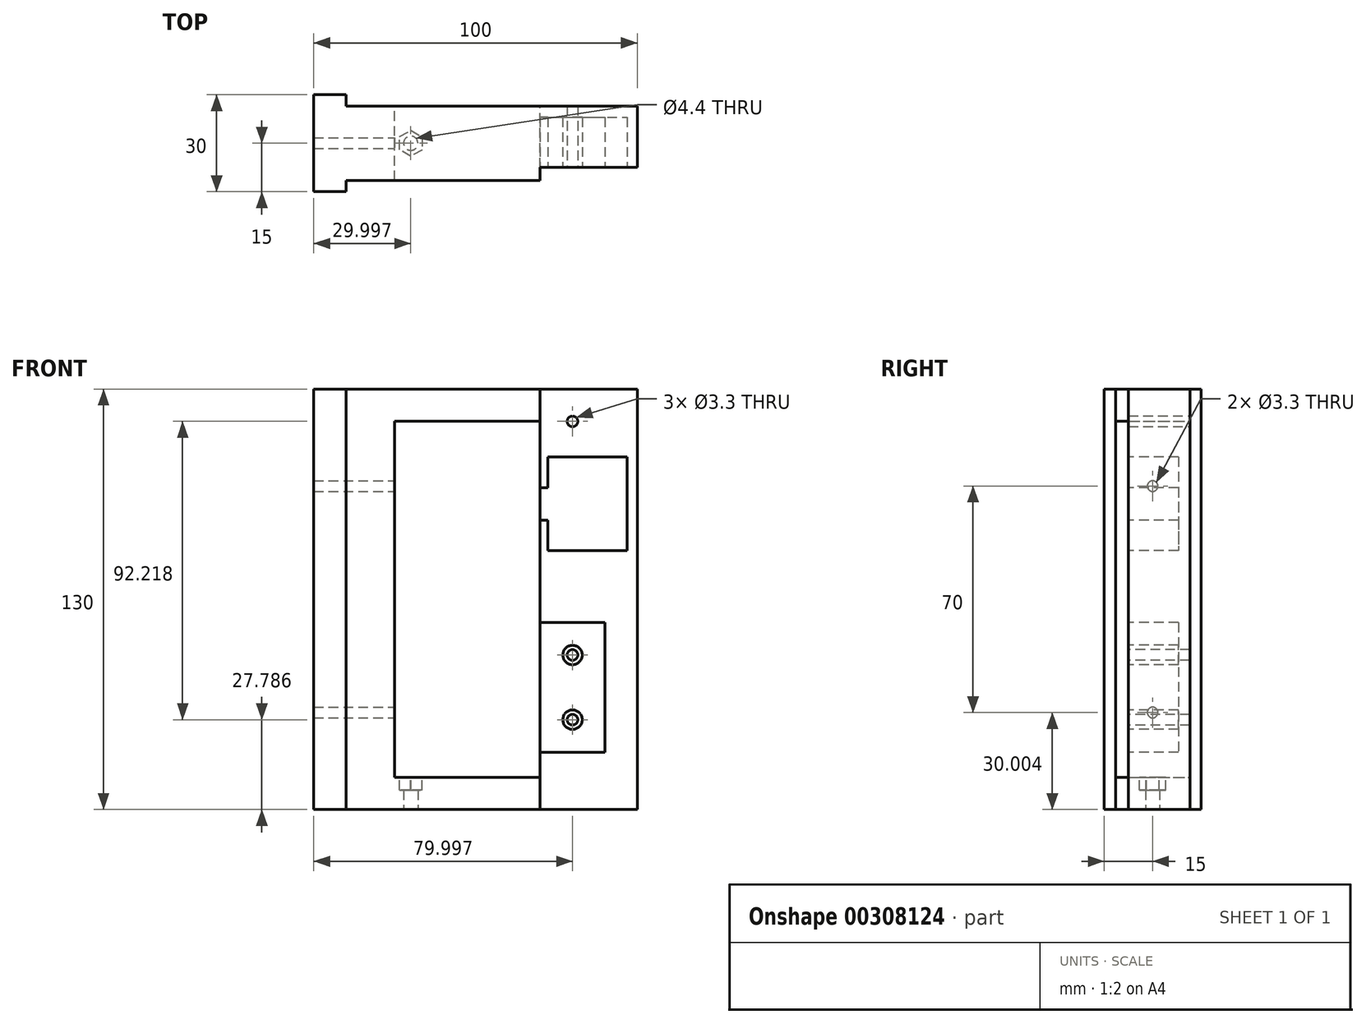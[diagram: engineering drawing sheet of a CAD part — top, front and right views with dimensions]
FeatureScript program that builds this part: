
annotation { "Feature Type Name" : "Feature", "Feature Type Description" : "" }
export const myFeature = defineFeature(function(context is Context, id is Id, definition is map)
    precondition{}
    {
        {
            var Q0;
            Q0=qCreatedBy(makeId("Front.planeOp"),FACE);
            var sketch = newSketch(context, id + "F0", { "sketchPlane" : qUnion([Q0])});
            skLineSegment(sketch, "E0", {"start": v(-34.7, 86.92) * mm, "end": v(-34.7, -43.08) * mm});
            skLineSegment(sketch, "E1", {"start": v(-34.7, -43.08) * mm, "end": v(55.3, -43.08) * mm});
            skLineSegment(sketch, "E2", {"start": v(55.3, -43.08) * mm, "end": v(55.3, 86.92) * mm});
            skLineSegment(sketch, "E3", {"start": v(55.3, 86.92) * mm, "end": v(-34.7, 86.92) * mm});
            skLineSegment(sketch, "E4.bottom", {"start": v(-19.7, 76.92) * mm, "end": v(25.3, 76.92) * mm});
            skLineSegment(sketch, "E4.top", {"start": v(-19.7, -33.08) * mm, "end": v(25.3, -33.08) * mm});
            skLineSegment(sketch, "E4.left", {"start": v(-19.7, 76.92) * mm, "end": v(-19.7, -33.08) * mm});
            skLineSegment(sketch, "E4.right", {"start": v(25.3, 76.92) * mm, "end": v(25.3, -33.08) * mm});
            skSolve(sketch);
        }
        {
            var Q0;
            Q0=makeQuery(id+"F0.imprint","IMPRINT",FACE,{"disambiguationData":[TD([[makeQuery(id+"F0.imprint","IMPRINT",EDGE,{"derivedFrom":sQuery(id+"F0.wireOp",EDGE,"E0")}),1.0]])]});
            extrude(context, id + "F1", {"entities" : qUnion([Q0]), "depth" : 23 * mm});
        }
        {
            var Q0;
            Q0=makeQuery(id+"F1.opExtrude","SWEPT_FACE",FACE,{"disambiguationData":[OSD([sQuery(id+"F0.wireOp",EDGE,"E0")])]});
            var sketch = newSketch(context, id + "F2", { "sketchPlane" : qUnion([Q0])});
            skLineSegment(sketch, "E5", {"start": v(23, 86.92) * mm, "end": v(26.5, 86.92) * mm});
            skLineSegment(sketch, "E6", {"start": v(26.5, 86.92) * mm, "end": v(26.5, -43.08) * mm});
            skLineSegment(sketch, "E7", {"start": v(26.5, -43.08) * mm, "end": v(23, -43.08) * mm});
            skLineSegment(sketch, "E8", {"start": v(23, -43.08) * mm, "end": v(0, -43.08) * mm});
            skLineSegment(sketch, "E9", {"start": v(0, -43.08) * mm, "end": v(-3.5, -43.08) * mm});
            skLineSegment(sketch, "E10", {"start": v(-3.5, -43.08) * mm, "end": v(-3.5, 86.92) * mm});
            skLineSegment(sketch, "E11", {"start": v(-3.5, 86.92) * mm, "end": v(0, 86.92) * mm});
            skSolve(sketch);
        }
        {
            var Q0;
            Q0=makeQuery(id+"F2.imprint","IMPRINT",FACE,{"disambiguationData":[TD([[makeQuery(id+"F2.imprint","IMPRINT",EDGE,{"derivedFrom":sQuery(id+"F2.wireOp",EDGE,"E9")}),-1.0]])]});
            var Q1;
            Q1=makeQuery(id+"F2.imprint","IMPRINT",FACE,{"disambiguationData":[TD([[makeQuery(id+"F2.imprint","IMPRINT",EDGE,{"derivedFrom":sQuery(id+"F2.wireOp",EDGE,"E8")}),-1.0]])]});
            var Q2;
            Q2=makeQuery(id+"F2.imprint","IMPRINT",FACE,{"disambiguationData":[TD([[makeQuery(id+"F2.imprint","IMPRINT",EDGE,{"derivedFrom":sQuery(id+"F2.wireOp",EDGE,"E5")}),-1.0]])]});
            extrude(context, id + "F3", {"entities" : qUnion([Q0, Q1, Q2]), "operationType" : NewBodyOperationType.ADD, "depth" : 10 * mm});
        }
        {
            var Q0;
            Q0=makeQuery(id+"F1.opExtrude","CAP_FACE",FACE,{"disambiguationData":[OSD([sQuery(id+"F0.wireOp",EDGE,"E0"),sQuery(id+"F0.wireOp",EDGE,"E1"),sQuery(id+"F0.wireOp",EDGE,"E2"),sQuery(id+"F0.wireOp",EDGE,"E3"),sQuery(id+"F0.wireOp",EDGE,"E4.bottom"),sQuery(id+"F0.wireOp",EDGE,"E4.top"),sQuery(id+"F0.wireOp",EDGE,"E4.left"),sQuery(id+"F0.wireOp",EDGE,"E4.right")])],"isStart":false});
            var sketch = newSketch(context, id + "F4", { "sketchPlane" : qUnion([Q0])});
            skLineSegment(sketch, "E12.bottom", {"start": v(55.3, 86.92) * mm, "end": v(25.3, 86.92) * mm});
            skLineSegment(sketch, "E12.top", {"start": v(55.3, -43.08) * mm, "end": v(25.3, -43.08) * mm});
            skLineSegment(sketch, "E12.left", {"start": v(55.3, 86.92) * mm, "end": v(55.3, -43.08) * mm});
            skLineSegment(sketch, "E12.right", {"start": v(25.3, 86.92) * mm, "end": v(25.3, -43.08) * mm});
            skSolve(sketch);
        }
        {
            var Q0;
            {var subQ2=sQuery(id+"F4.wireOp",EDGE,"E12.bottom");Q0=makeQuery(id+"F4.imprint","IMPRINT",FACE,{"disambiguationData":[TD([[makeQuery(id+"F4.imprint","IMPRINT",EDGE,{"derivedFrom":subQ2}),1.0]])]});}
            extrude(context, id + "F5", {"entities" : qUnion([Q0]), "operationType" : NewBodyOperationType.REMOVE, "oppositeDirection" : true, "depth" : 4 * mm});
        }
        {
            var Q0;
            Q0=makeQuery(id+"F5.boolean.opBoolean","COPY",FACE,{"derivedFrom":makeQuery(id+"F5.opExtrude","CAP_FACE",FACE,{"disambiguationData":[OSD([sQuery(id+"F4.wireOp",EDGE,"E12.bottom"),sQuery(id+"F4.wireOp",EDGE,"E12.top"),sQuery(id+"F4.wireOp",EDGE,"E12.left"),sQuery(id+"F4.wireOp",EDGE,"E12.right")])],"isStart":false})});
            var sketch = newSketch(context, id + "F6", { "sketchPlane" : qUnion([Q0])});
            skLineSegment(sketch, "E13.bottom", {"start": v(27.63, 65.92) * mm, "end": v(52.13, 65.92) * mm});
            skLineSegment(sketch, "E13.top", {"start": v(27.63, 36.92) * mm, "end": v(52.13, 36.92) * mm});
            skLineSegment(sketch, "E13.left", {"start": v(27.63, 65.92) * mm, "end": v(27.63, 36.92) * mm});
            skLineSegment(sketch, "E13.right", {"start": v(52.13, 65.92) * mm, "end": v(52.13, 36.92) * mm});
            skLineSegment(sketch, "E14.bottom", {"start": v(33.13, 56.42) * mm, "end": v(22.13, 56.42) * mm});
            skLineSegment(sketch, "E14.top", {"start": v(33.13, 46.42) * mm, "end": v(22.13, 46.42) * mm});
            skLineSegment(sketch, "E14.left", {"start": v(33.13, 56.42) * mm, "end": v(33.13, 46.42) * mm});
            skLineSegment(sketch, "E14.right", {"start": v(22.13, 56.42) * mm, "end": v(22.13, 46.42) * mm});
            skPoint(sketch, "E14.middle", {"position": v(27.63, 51.42) * mm});
            skLineSegment(sketch, "E15.bottom", {"start": v(52.13, 36.92) * mm, "end": v(42.13, 36.92) * mm});
            skLineSegment(sketch, "E15.top", {"start": v(52.13, 26.92) * mm, "end": v(42.13, 26.92) * mm});
            skLineSegment(sketch, "E15.left", {"start": v(52.13, 36.92) * mm, "end": v(52.13, 26.92) * mm});
            skLineSegment(sketch, "E15.right", {"start": v(42.13, 36.92) * mm, "end": v(42.13, 26.92) * mm});
            skLineSegment(sketch, "E16.bottom", {"start": v(52.13, 65.92) * mm, "end": v(42.13, 65.92) * mm});
            skLineSegment(sketch, "E16.top", {"start": v(52.13, 75.92) * mm, "end": v(42.13, 75.92) * mm});
            skLineSegment(sketch, "E16.left", {"start": v(52.13, 65.92) * mm, "end": v(52.13, 75.92) * mm});
            skLineSegment(sketch, "E16.right", {"start": v(42.13, 65.92) * mm, "end": v(42.13, 75.92) * mm});
            skLineSegment(sketch, "E17.bottom", {"start": v(25.3, 14.76) * mm, "end": v(45.3, 14.76) * mm});
            skLineSegment(sketch, "E17.top", {"start": v(25.3, -25.34) * mm, "end": v(45.3, -25.34) * mm});
            skLineSegment(sketch, "E17.left", {"start": v(25.3, 14.76) * mm, "end": v(25.3, -25.34) * mm});
            skLineSegment(sketch, "E17.right", {"start": v(45.3, 14.76) * mm, "end": v(45.3, -25.34) * mm});
            skCircle(sketch, "E18", {"center": v(35.3, 4.7) * mm, "radius": 3 * mm});
            skCircle(sketch, "E19", {"center": v(35.3, -15.3) * mm, "radius": 3 * mm});
            skLineSegment(sketch, "E20", {"start": v(45.3, -5.3) * mm, "end": v(25.3, -5.3) * mm, "construction": true});
            skSolve(sketch);
        }
        {
            var Q0;
            {var subQ4=sQuery(id+"F6.wireOp",EDGE,"E13.bottom");Q0=makeQuery(id+"F6.imprint","IMPRINT",FACE,{"disambiguationData":[TD([[makeQuery(id+"F6.imprint","IMPRINT",EDGE,{"derivedFrom":subQ4}),-1.0]])]});}
            var Q1;
            {var subQ5=sQuery(id+"F6.wireOp",EDGE,"E14.left");Q1=makeQuery(id+"F6.imprint","IMPRINT",FACE,{"disambiguationData":[TD([[makeQuery(id+"F6.imprint","IMPRINT",EDGE,{"derivedFrom":subQ5}),-1.0]])]});}
            var Q2;
            {var subQ0=sQuery(id+"F6.wireOp",EDGE,"E14.right");Q2=makeQuery(id+"F6.imprint","IMPRINT",FACE,{"disambiguationData":[TD([[makeQuery(id+"F6.imprint","IMPRINT",EDGE,{"derivedFrom":subQ0}),1.0]])]});}
            var Q3;
            {var subQ0=sQuery(id+"F6.wireOp",EDGE,"E14.bottom");var subQ1=sQuery(id+"F6.wireOp",EDGE,"E13.left");var subQ2=makeQuery(id+"F6.imprint","INTERSECT",VERTEX,{"derivedFrom":[subQ1,subQ0]});Q3=makeQuery(id+"F6.imprint","IMPRINT",FACE,{"disambiguationData":[TD([[makeQuery(id+"F6.imprint","IMPRINT",EDGE,{"disambiguationData":[TD([[subQ2,-1.0]])],"derivedFrom":subQ1}),-1.0]])]});}
            var Q4;
            Q4=makeQuery(id+"F6.imprint","IMPRINT",FACE,{"disambiguationData":[TD([[makeQuery(id+"F6.imprint","IMPRINT",EDGE,{"derivedFrom":sQuery(id+"F6.wireOp",EDGE,"E16.bottom")}),-1.0]])]});
            var Q5;
            Q5=makeQuery(id+"F6.imprint","IMPRINT",FACE,{"disambiguationData":[TD([[makeQuery(id+"F6.imprint","IMPRINT",EDGE,{"derivedFrom":sQuery(id+"F6.wireOp",EDGE,"E15.bottom")}),1.0]])]});
            var Q6;
            Q6=makeQuery(id+"F6.imprint","IMPRINT",FACE,{"disambiguationData":[TD([[makeQuery(id+"F6.imprint","IMPRINT",EDGE,{"derivedFrom":sQuery(id+"F6.wireOp",EDGE,"E17.bottom")}),-1.0]])]});
            extrude(context, id + "F7", {"entities" : qUnion([Q0, Q1, Q2, Q3, Q4, Q5, Q6]), "operationType" : NewBodyOperationType.REMOVE, "oppositeDirection" : true, "depth" : 15.5 * mm});
        }
        {
            var Q0;
            Q0=makeQuery(id+"F0.imprint","IMPRINT",FACE,{"disambiguationData":[TD([[makeQuery(id+"F0.imprint","IMPRINT",EDGE,{"derivedFrom":sQuery(id+"F0.wireOp",EDGE,"E0")}),1.0]])]});
            var sketch = newSketch(context, id + "F8", { "sketchPlane" : qUnion([Q0])});
            skPoint(sketch, "E21.0", {"position": v(35.3, -15.3) * mm});
            skLineSegment(sketch, "E22", {"start": v(35.3, -15.3) * mm, "end": v(35.3, 86.3) * mm, "construction": true});
            skPoint(sketch, "E23", {"position": v(35.3, 76.92) * mm});
            skSolve(sketch);
        }
        {
            var Q0;
            Q0=sQuery(id+"F6.wireOp",VERTEX,"E18.center");
            var Q1;
            Q1=sQuery(id+"F6.wireOp",VERTEX,"E19.center");
            var Q2;
            Q2=makeQuery(id+"F1.opExtrude","SWEPT_BODY",BODY,{"disambiguationData":[OSD([sQuery(id+"F0.wireOp",EDGE,"E0"),sQuery(id+"F0.wireOp",EDGE,"E1"),sQuery(id+"F0.wireOp",EDGE,"E2"),sQuery(id+"F0.wireOp",EDGE,"E3"),sQuery(id+"F0.wireOp",EDGE,"E4.bottom"),sQuery(id+"F0.wireOp",EDGE,"E4.top"),sQuery(id+"F0.wireOp",EDGE,"E4.left"),sQuery(id+"F0.wireOp",EDGE,"E4.right")])]});
            hole(context, id + "F9", {"style" : HoleStyle.SIMPLE, "endStyle" : HoleEndStyle.BLIND, "standardTappedOrClearance" : lookupTablePath({ "standard" : "ISO", "fit" : "Normal", "size" : "M3", "type" : "Clearance" }), "standardBlindInLast" : lookupTablePath({ "fit" : "Standard", "standard" : "ISO", "size" : "M3", "type" : "Clearance" }), "holeDiameter" : 3.3 * mm, "holeDepth" : 40 * mm, "isTappedThrough" : true, "tappedDepth" : 12 * mm, "tapClearance" : 3, "locations" : qUnion([Q0, Q1]), "scope" : qUnion([Q2])});
        }
        {
            var Q0;
            Q0=sQuery(id+"F8.wireOp",VERTEX,"E23");
            var Q1;
            Q1=makeQuery(id+"F1.opExtrude","SWEPT_BODY",BODY,{"disambiguationData":[OSD([sQuery(id+"F0.wireOp",EDGE,"E0"),sQuery(id+"F0.wireOp",EDGE,"E1"),sQuery(id+"F0.wireOp",EDGE,"E2"),sQuery(id+"F0.wireOp",EDGE,"E3"),sQuery(id+"F0.wireOp",EDGE,"E4.bottom"),sQuery(id+"F0.wireOp",EDGE,"E4.top"),sQuery(id+"F0.wireOp",EDGE,"E4.left"),sQuery(id+"F0.wireOp",EDGE,"E4.right")])]});
            hole(context, id + "F10", {"style" : HoleStyle.SIMPLE, "endStyle" : HoleEndStyle.BLIND, "oppositeDirection" : true, "standardTappedOrClearance" : lookupTablePath({ "standard" : "ISO", "fit" : "Normal", "size" : "M3", "type" : "Clearance" }), "standardBlindInLast" : lookupTablePath({ "fit" : "Standard", "standard" : "ISO", "size" : "M3", "type" : "Clearance" }), "holeDiameter" : 3.3 * mm, "holeDepth" : 40 * mm, "isTappedThrough" : true, "tappedDepth" : 12 * mm, "tapClearance" : 3, "locations" : qUnion([Q0]), "scope" : qUnion([Q1])});
        }
        {
            var Q0;
            Q0=makeQuery(id+"F1.opExtrude","SWEPT_FACE",FACE,{"disambiguationData":[OSD([sQuery(id+"F0.wireOp",EDGE,"E4.left")])]});
            var sketch = newSketch(context, id + "F11", { "sketchPlane" : qUnion([Q0])});
            skPoint(sketch, "E24", {"position": v(-11.5, 56.92) * mm});
            skPoint(sketch, "E25", {"position": v(-11.5, -13.08) * mm});
            skSolve(sketch);
        }
        {
            var Q0;
            Q0=sQuery(id+"F11.wireOp",VERTEX,"E24");
            var Q1;
            Q1=sQuery(id+"F11.wireOp",VERTEX,"E25");
            var Q2;
            Q2=makeQuery(id+"F1.opExtrude","SWEPT_BODY",BODY,{"disambiguationData":[OSD([sQuery(id+"F0.wireOp",EDGE,"E0"),sQuery(id+"F0.wireOp",EDGE,"E1"),sQuery(id+"F0.wireOp",EDGE,"E2"),sQuery(id+"F0.wireOp",EDGE,"E3"),sQuery(id+"F0.wireOp",EDGE,"E4.bottom"),sQuery(id+"F0.wireOp",EDGE,"E4.top"),sQuery(id+"F0.wireOp",EDGE,"E4.left"),sQuery(id+"F0.wireOp",EDGE,"E4.right")])]});
            hole(context, id + "F12", {"style" : HoleStyle.SIMPLE, "endStyle" : HoleEndStyle.BLIND, "standardTappedOrClearance" : lookupTablePath({ "standard" : "ISO", "fit" : "Normal", "size" : "M3", "type" : "Clearance" }), "standardBlindInLast" : lookupTablePath({ "fit" : "Standard", "standard" : "ISO", "size" : "M3", "type" : "Clearance" }), "holeDiameter" : 3.3 * mm, "holeDepth" : 40 * mm, "isTappedThrough" : true, "tappedDepth" : 12 * mm, "tapClearance" : 3, "locations" : qUnion([Q0, Q1]), "scope" : qUnion([Q2])});
        }
        {
            var Q0;
            Q0=makeQuery(id+"F3.boolean.opBoolean","MERGE",FACE,{"derivedFrom":[makeQuery(id+"F1.opExtrude","SWEPT_FACE",FACE,{"disambiguationData":[OSD([sQuery(id+"F0.wireOp",EDGE,"E1")])]}),makeQuery(id+"F3.opExtrude","SWEPT_FACE",FACE,{"disambiguationData":[OSD([sQuery(id+"F2.wireOp",EDGE,"E7"),sQuery(id+"F2.wireOp",EDGE,"E8"),sQuery(id+"F2.wireOp",EDGE,"E9")])]})]});
            var sketch = newSketch(context, id + "F13", { "sketchPlane" : qUnion([Q0])});
            skLineSegment(sketch, "E26", {"start": v(-44.7, 11.5) * mm, "end": v(55.3, 11.5) * mm, "construction": true});
            skPoint(sketch, "E27", {"position": v(-14.7, 11.5) * mm});
            skSolve(sketch);
        }
        {
            var Q0;
            Q0=sQuery(id+"F13.wireOp",VERTEX,"E27");
            var Q1;
            Q1=makeQuery(id+"F1.opExtrude","SWEPT_BODY",BODY,{"disambiguationData":[OSD([sQuery(id+"F0.wireOp",EDGE,"E0"),sQuery(id+"F0.wireOp",EDGE,"E1"),sQuery(id+"F0.wireOp",EDGE,"E2"),sQuery(id+"F0.wireOp",EDGE,"E3"),sQuery(id+"F0.wireOp",EDGE,"E4.bottom"),sQuery(id+"F0.wireOp",EDGE,"E4.top"),sQuery(id+"F0.wireOp",EDGE,"E4.left"),sQuery(id+"F0.wireOp",EDGE,"E4.right")])]});
            hole(context, id + "F14", {"style" : HoleStyle.SIMPLE, "endStyle" : HoleEndStyle.BLIND, "standardTappedOrClearance" : lookupTablePath({ "standard" : "ISO", "fit" : "Normal", "size" : "M4", "type" : "Clearance" }), "standardBlindInLast" : lookupTablePath({ "fit" : "Standard", "standard" : "ISO", "size" : "M4", "type" : "Clearance" }), "holeDiameter" : 4.4 * mm, "holeDepth" : 10 * mm, "tappedDepth" : 12 * mm, "tapClearance" : 3, "locations" : qUnion([Q0]), "scope" : qUnion([Q1])});
        }
        {
            var Q0;
            Q0=makeQuery(id+"F1.opExtrude","SWEPT_FACE",FACE,{"disambiguationData":[OSD([sQuery(id+"F0.wireOp",EDGE,"E4.top")])]});
            var sketch = newSketch(context, id + "F15", { "sketchPlane" : qUnion([Q0])});
            skCircle(sketch, "E28.cCircle", {"center": v(-14.7, -11.5) * mm, "radius": 3.5 * mm, "construction": true});
            skLineSegment(sketch, "E28.0", {"start": v(-14.65, -7.46) * mm, "end": v(-11.18, -9.52) * mm});
            skLineSegment(sketch, "E28.1", {"start": v(-11.18, -9.52) * mm, "end": v(-11.23, -13.57) * mm});
            skLineSegment(sketch, "E28.2", {"start": v(-11.23, -13.57) * mm, "end": v(-14.76, -15.54) * mm});
            skLineSegment(sketch, "E28.3", {"start": v(-14.76, -15.54) * mm, "end": v(-18.23, -13.48) * mm});
            skLineSegment(sketch, "E28.4", {"start": v(-18.23, -13.48) * mm, "end": v(-18.18, -9.43) * mm});
            skLineSegment(sketch, "E28.5", {"start": v(-18.18, -9.43) * mm, "end": v(-14.65, -7.46) * mm});
            skPoint(sketch, "E28.0.midPoint", {"position": v(-12.91, -8.5) * mm});
            skSolve(sketch);
        }
        {
            var Q0;
            Q0=makeQuery(id+"F15.imprint","IMPRINT",FACE,{"disambiguationData":[TD([[makeQuery(id+"F15.imprint","IMPRINT",EDGE,{"derivedFrom":sQuery(id+"F15.wireOp",EDGE,"E28.0")}),-1.0]])]});
            extrude(context, id + "F16", {"entities" : qUnion([Q0]), "operationType" : NewBodyOperationType.REMOVE, "oppositeDirection" : true, "depth" : 4 * mm});
        }
    });
